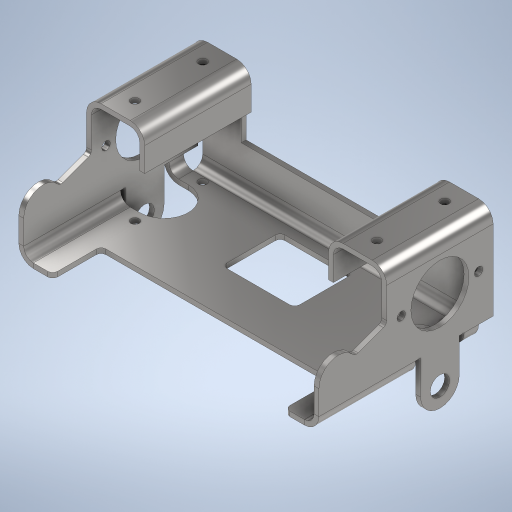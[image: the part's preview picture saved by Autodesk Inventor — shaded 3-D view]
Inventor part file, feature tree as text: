
AUTODESK INVENTOR PART (.ipt)
format: ipt  version: 2024 (Build 280153000, 153)  size: 628,224 bytes
history: native  units: mm
features: sheet_metal_op x25, other x18, sketch x17, extrude x1, plane x1, mirror x1
ambient origin geometry x8: Origin, YZ Plane, XZ Plane, XY Plane, X Axis, Y Axis, Z Axis, Center Point
bodies: Solid1 (feature_tree)
feature tree (63):
  sheet_metal_op  "Face1"
  sheet_metal_op  "Flange1"
  sheet_metal_op  "Flange2"
  sheet_metal_op  "Flange3"
  sheet_metal_op  "Flange4"
  sheet_metal_op  "Flange5"
  sheet_metal_op  "Flange6"
  sheet_metal_op  "Flange7"
  other  "Full Round Fillet1"
  other  "Full Round Fillet2"
  sheet_metal_op  "Flange8"
  extrude  "Extrusion1"  Depth=124.0mm
  plane  "Work Plane1"
  mirror  "Mirror1"
  sketch  "Sketch1"  dims[d0=72.0mm d1=124.0mm]
  other  "Plate1"
  sketch  "Sketch2"  dims[d2=14.0mm]
  other  "Plate2"
  sheet_metal_op  "Bend1"
  sheet_metal_op  "Corner1"
  sketch  "Sketch3"  dims[d3=20.0mm]
  other  "Plate3"
  sheet_metal_op  "Bend2"
  sheet_metal_op  "Corner2"
  sketch  "Sketch4"  dims[d4=96.0mm]
  other  "Plate4"
  sheet_metal_op  "Bend3"
  sheet_metal_op  "Corner3"
  sketch  "Sketch5"  dims[d5=24.0mm]
  other  "Plate5"
  sheet_metal_op  "Bend4"
  sheet_metal_op  "Corner4"
  sketch  "Sketch6"  dims[d6=30.0mm]
  other  "Plate6"
  sheet_metal_op  "Bend5"
  sheet_metal_op  "Corner5"
  sketch  "Sketch7"  dims[d7=2.0mm]
  other  "Plate7"
  sheet_metal_op  "Bend6"
  sheet_metal_op  "Corner6"
  sketch  "Sketch10"  dims[d8=2.0mm]
  sketch  "Sketch11"  dims[d9=22.0mm]
  other  "Plate8"
  sheet_metal_op  "Bend7"
  sheet_metal_op  "Corner7"
  sketch  "Sketch12"  dims[d10=2.0mm]
  sketch  "Sketch13"  dims[d11=2.0mm]
  sketch  "Sketch14"  dims[d12=1.0mm]
  other  "Plate9"
  sheet_metal_op  "Bend8"
  sheet_metal_op  "Corner8"
  sketch  "Sketch16"  dims[d13=4.0mm]
  sketch  "Sketch17"  dims[d14=2.0mm]
  sketch  "Sketch18"  dims[d15=45.0mm d16=90.0deg d17=4.0mm]
  sketch  "Sketch19"  dims[d18=8.0mm]
  sketch  "Sketch20"  dims[d19=2.0mm d20=2.0mm d21=2.0mm d22=1.0mm d23=4.0mm d24=2.0mm d25=45.0mm d26=90.0deg d27=4.0mm d28=8.0mm d29=2.0mm d30=2.0mm d31=2.0mm d32=1.0mm d33=4.0mm d34=2.0mm d35=24.0mm d36=90.0deg d37=4.0mm d38=8.0mm d39=2.0mm d40=2.0mm d41=2.0mm d42=1.0mm d43=4.0mm d44=2.0mm d45=24.0mm d46=90.0deg d47=4.0mm d48=8.0mm d49=2.0mm d50=2.0mm d51=2.0mm d52=1.0mm d53=4.0mm d54=2.0mm d55=16.0mm d56=90.0deg d57=4.0mm d58=8.0mm d59=2.0mm d60=2.0mm d61=2.0mm d62=1.0mm d63=4.0mm d64=2.0mm d65=16.0mm d66=90.0deg d67=4.0mm d68=8.0mm d69=2.0mm d70=2.0mm d71=10.0mm d72=20.0mm d73=22.0mm d74=20.0mm d75=10.0mm d76=10.0mm d77=22.0mm d78=6.0mm d79=0.0mm d80=2.0mm d81=1.0mm d82=4.0mm d83=2.0mm d84=22.0mm d85=0.0mm d86=0.0mm d87=8.0mm d88=2.0mm d89=2.0mm d90=44.0mm d91=20.0mm d93=27.925268mm d94=16.0mm d95=16.0mm d96=2.0mm d97=2.0mm d98=124.0mm d99=0.0mm d100=8.0mm d101=8.0mm d102=8.0mm d103=124.0mm d104=0.0mm d105=2.0mm d106=1.0mm d107=4.0mm d108=2.0mm d109=18.0mm d110=90.0deg d111=4.0mm d112=8.0mm d113=2.0mm d114=2.0mm d115=0.1mm d116=0.1mm d117=0.1mm d118=2.0mm d119=0.0mm d120=36.0mm d121=2.0mm d122=0.0mm d123=4.0mm d124=36.0mm d125=2.0mm d126=0.0mm d127=3.5mm d128=8.0mm d129=12.0mm d130=3.5mm d131=36.0mm d132=3.5mm d133=3.5mm d134=12.0mm d135=12.0mm d136=50.0mm d137=0.0mm d138=24.0mm d139=25.0mm d140=3.5mm d141=3.5mm d142=16.0mm d143=16.0mm d144=2.0mm d145=0.0mm d146=-62.0mm]
  other  "Cut1"
  other  "Cut2"
  other  "Cut3"
  other  "Cut4"
  other  "Cut5"
  other  "Cut6"
  other  "Cut7"
